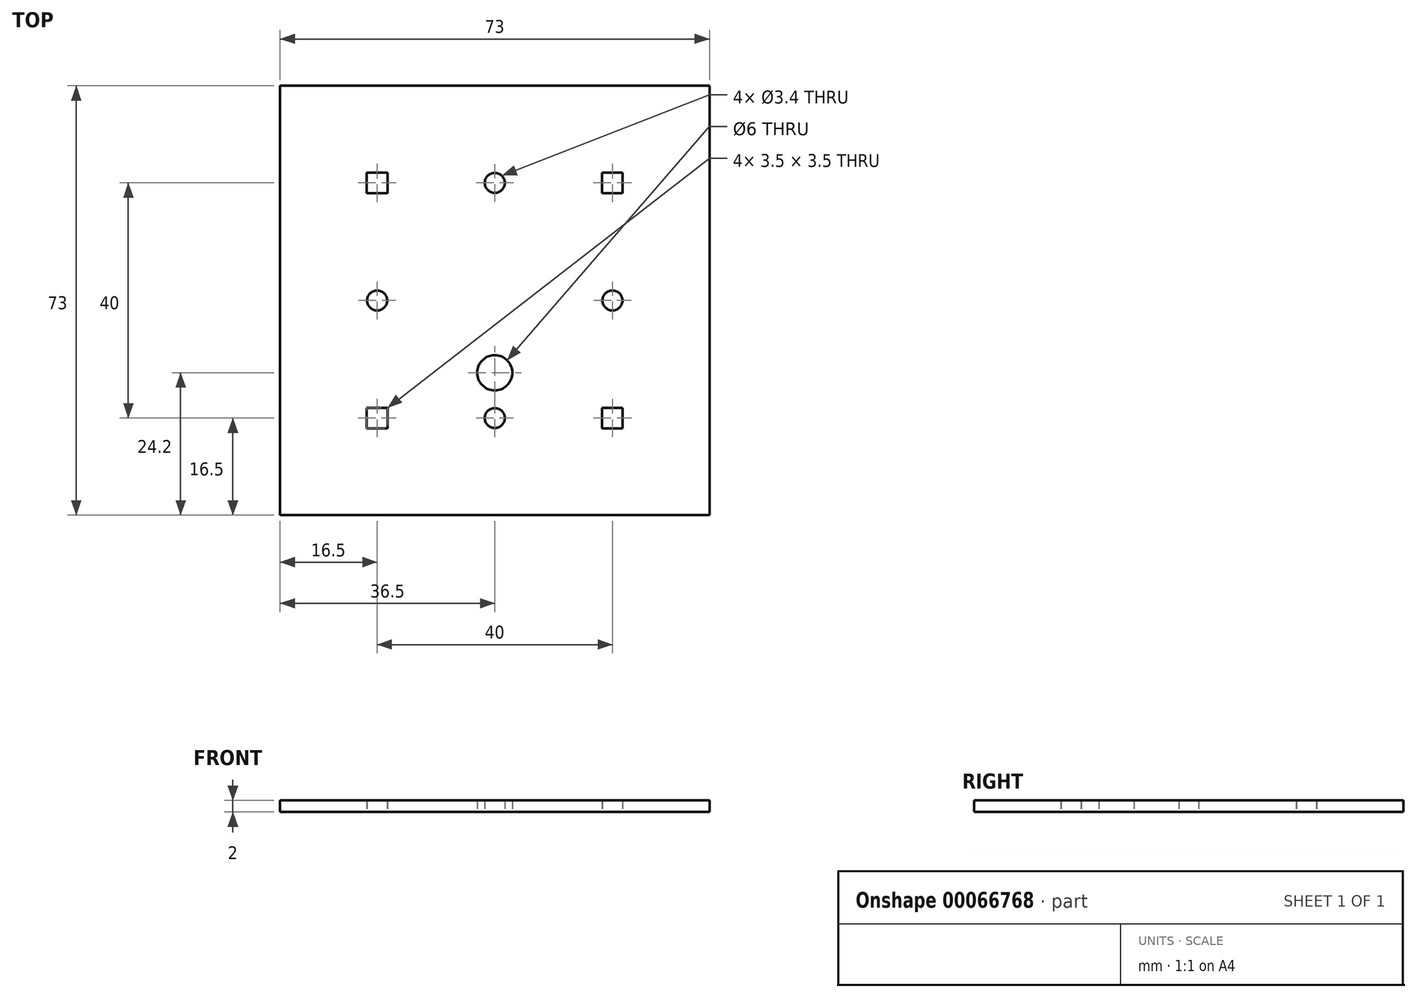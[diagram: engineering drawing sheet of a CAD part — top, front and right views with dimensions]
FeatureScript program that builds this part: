
annotation { "Feature Type Name" : "Feature", "Feature Type Description" : "" }
export const myFeature = defineFeature(function(context is Context, id is Id, definition is map)
    precondition{}
    {
        {
            var Q0;
            Q0=qCreatedBy(makeId("Top.planeOp"),FACE);
            var sketch = newSketch(context, id + "F0", { "sketchPlane" : qUnion([Q0])});
            skLineSegment(sketch, "E0", {"start": v(36.5, 0) * mm, "end": v(36.5, -36.5) * mm});
            skLineSegment(sketch, "E1", {"start": v(36.5, -36.5) * mm, "end": v(0, -36.5) * mm});
            skLineSegment(sketch, "E2", {"start": v(0, -20) * mm, "end": v(20, -20) * mm, "construction": true});
            skLineSegment(sketch, "E3", {"start": v(20, 0) * mm, "end": v(20, -20) * mm, "construction": true});
            skLineSegment(sketch, "E4.MirrorCS", {"start": v(-20, 0) * mm, "end": v(-20, -20) * mm, "construction": true});
            skLineSegment(sketch, "E5.MirrorCS", {"start": v(0, -20) * mm, "end": v(-20, -20) * mm, "construction": true});
            skLineSegment(sketch, "E6.MirrorCS", {"start": v(-36.5, -36.5) * mm, "end": v(0, -36.5) * mm});
            skLineSegment(sketch, "E7.MirrorCS", {"start": v(-36.5, 0) * mm, "end": v(-36.5, -36.5) * mm});
            skLineSegment(sketch, "E8.MirrorCS", {"start": v(-36.5, 0) * mm, "end": v(-36.5, 36.5) * mm});
            skLineSegment(sketch, "E9.MirrorCS", {"start": v(-20, 0) * mm, "end": v(-20, 20) * mm, "construction": true});
            skLineSegment(sketch, "E10.MirrorCS", {"start": v(20, 0) * mm, "end": v(20, 20) * mm, "construction": true});
            skLineSegment(sketch, "E11.MirrorCS", {"start": v(36.5, 0) * mm, "end": v(36.5, 36.5) * mm});
            skLineSegment(sketch, "E12.MirrorCS", {"start": v(-36.5, 36.5) * mm, "end": v(0, 36.5) * mm});
            skLineSegment(sketch, "E13.MirrorCS", {"start": v(36.5, 36.5) * mm, "end": v(0, 36.5) * mm});
            skLineSegment(sketch, "E14.MirrorCS", {"start": v(0, 20) * mm, "end": v(-20, 20) * mm, "construction": true});
            skLineSegment(sketch, "E15.MirrorCS", {"start": v(0, 20) * mm, "end": v(20, 20) * mm, "construction": true});
            skCircle(sketch, "E16", {"center": v(0, -20) * mm, "radius": 1.7 * mm});
            skCircle(sketch, "E17", {"center": v(20, 0) * mm, "radius": 1.7 * mm});
            skCircle(sketch, "E18", {"center": v(0, 20) * mm, "radius": 1.7 * mm});
            skCircle(sketch, "E19", {"center": v(-20, 0) * mm, "radius": 1.7 * mm});
            skLineSegment(sketch, "E20", {"start": v(-21.75, 21.75) * mm, "end": v(-18.25, 21.75) * mm});
            skLineSegment(sketch, "E21", {"start": v(-18.25, 21.75) * mm, "end": v(-18.25, 18.25) * mm});
            skLineSegment(sketch, "E22", {"start": v(-18.25, 18.25) * mm, "end": v(-21.75, 18.25) * mm});
            skLineSegment(sketch, "E23", {"start": v(-21.75, 21.75) * mm, "end": v(-21.75, 18.25) * mm});
            skLineSegment(sketch, "E24.MirrorCS", {"start": v(21.75, 21.75) * mm, "end": v(21.75, 18.25) * mm});
            skLineSegment(sketch, "E25.MirrorCS", {"start": v(18.25, 18.25) * mm, "end": v(21.75, 18.25) * mm});
            skLineSegment(sketch, "E26.MirrorCS", {"start": v(21.75, 21.75) * mm, "end": v(18.25, 21.75) * mm});
            skLineSegment(sketch, "E27.MirrorCS", {"start": v(18.25, 21.75) * mm, "end": v(18.25, 18.25) * mm});
            skLineSegment(sketch, "E28.MirrorCS", {"start": v(18.25, -18.25) * mm, "end": v(21.75, -18.25) * mm});
            skLineSegment(sketch, "E29.MirrorCS", {"start": v(21.75, -21.75) * mm, "end": v(21.75, -18.25) * mm});
            skLineSegment(sketch, "E30.MirrorCS", {"start": v(21.75, -21.75) * mm, "end": v(18.25, -21.75) * mm});
            skLineSegment(sketch, "E31.MirrorCS", {"start": v(18.25, -21.75) * mm, "end": v(18.25, -18.25) * mm});
            skLineSegment(sketch, "E32.MirrorCS", {"start": v(-21.75, -21.75) * mm, "end": v(-21.75, -18.25) * mm});
            skLineSegment(sketch, "E33.MirrorCS", {"start": v(-18.25, -21.75) * mm, "end": v(-18.25, -18.25) * mm});
            skLineSegment(sketch, "E34.MirrorCS", {"start": v(-21.75, -21.75) * mm, "end": v(-18.25, -21.75) * mm});
            skLineSegment(sketch, "E35.MirrorCS", {"start": v(-18.25, -18.25) * mm, "end": v(-21.75, -18.25) * mm});
            skLineSegment(sketch, "E36", {"start": v(0, -20) * mm, "end": v(0, -12.3) * mm, "construction": true});
            skCircle(sketch, "E37", {"center": v(0, -12.3) * mm, "radius": 3 * mm});
            skSolve(sketch);
        }
        {
            var Q0;
            Q0=qSketchRegion(id+"F0",true);
            extrude(context, id + "F1", {"entities" : qUnion([Q0]), "depth" : 2 * mm});
        }
    });
